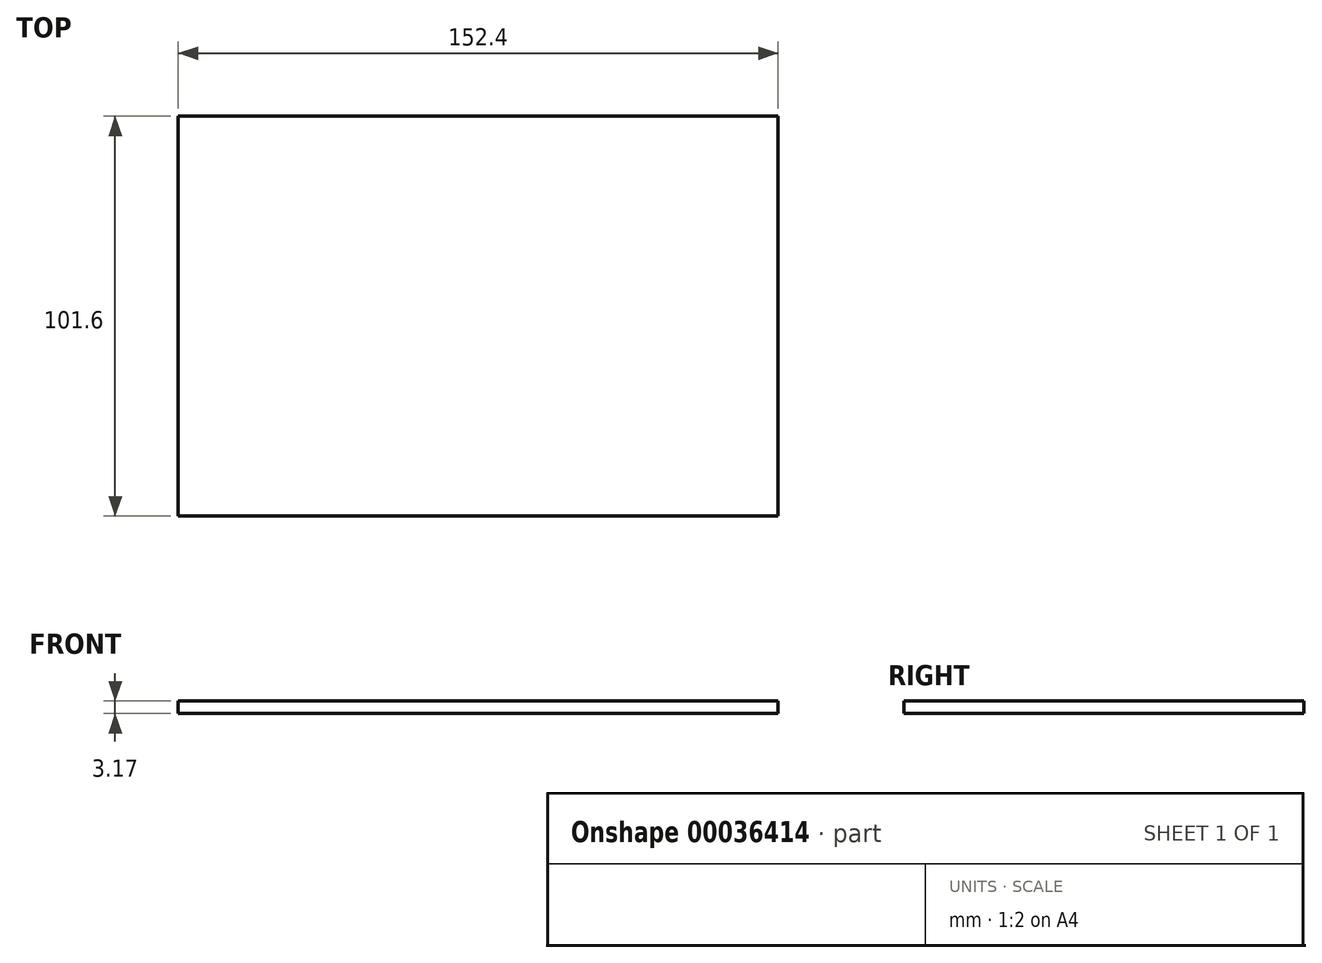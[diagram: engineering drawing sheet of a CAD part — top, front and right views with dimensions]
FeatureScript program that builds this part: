
annotation { "Feature Type Name" : "Feature", "Feature Type Description" : "" }
export const myFeature = defineFeature(function(context is Context, id is Id, definition is map)
    precondition{}
    {
        {
            var Q0;
            Q0=qCreatedBy(makeId("Top.planeOp"),FACE);
            var sketch = newSketch(context, id + "F0", { "sketchPlane" : qUnion([Q0])});
            skLineSegment(sketch, "E0.rect.bottom", {"start": v(76.2, -50.8) * mm, "end": v(-76.2, -50.8) * mm});
            skLineSegment(sketch, "E0.rect.top", {"start": v(76.2, 50.8) * mm, "end": v(-76.2, 50.8) * mm});
            skLineSegment(sketch, "E0.rect.left", {"start": v(76.2, -50.8) * mm, "end": v(76.2, 50.8) * mm});
            skLineSegment(sketch, "E0.rect.right", {"start": v(-76.2, -50.8) * mm, "end": v(-76.2, 50.8) * mm});
            skPoint(sketch, "E0.rect.middle", {"position": v(0, 0) * mm});
            skSolve(sketch);
        }
        {
            var Q0;
            Q0=makeQuery(id+"F0.imprint","IMPRINT",FACE,{"disambiguationData":[TD([[makeQuery(id+"F0.imprint","IMPRINT",EDGE,{"derivedFrom":sQuery(id+"F0.wireOp",EDGE,"E0.rect.bottom")}),-1.0]])]});
            extrude(context, id + "F1", {"entities" : qUnion([Q0]), "depth" : 3.17 * mm});
        }
    });
